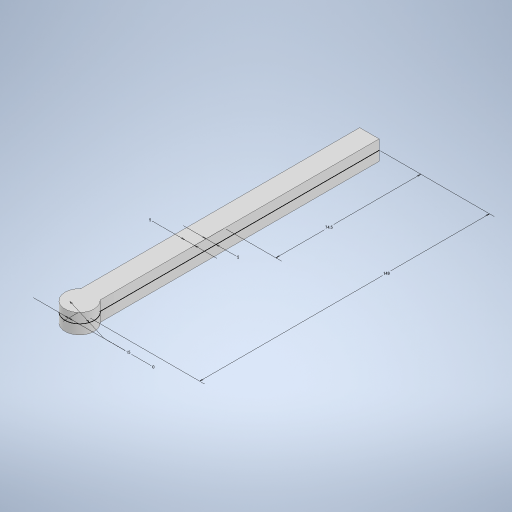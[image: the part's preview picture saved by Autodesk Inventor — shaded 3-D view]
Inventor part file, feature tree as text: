
AUTODESK INVENTOR PART (.ipt)
format: ipt  version: 2024.3 (Build 283343000, 343)  size: 246,784 bytes
history: native  units: mm
features: other x1, sketch x1, extrude x1
ambient origin geometry x8: Origin, YZ Plane, XZ Plane, XY Plane, X Axis, Y Axis, Z Axis, Center Point
bodies: Body1 (feature_tree)
feature tree (3):
  other  "ソリッド1"
  sketch  "スケッチ1"
  extrude  "押し出し1"  Depth=15.0mm
